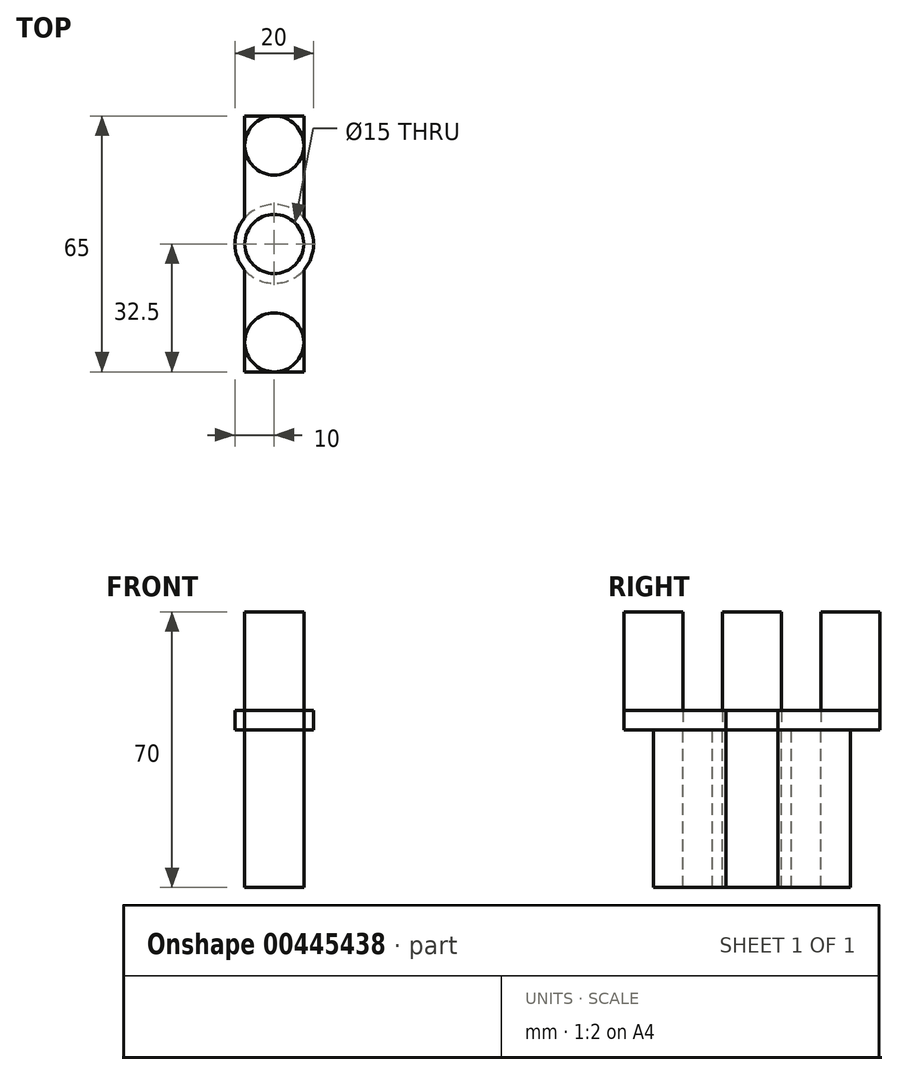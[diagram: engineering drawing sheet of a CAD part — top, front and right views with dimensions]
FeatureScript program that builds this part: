
annotation { "Feature Type Name" : "Feature", "Feature Type Description" : "" }
export const myFeature = defineFeature(function(context is Context, id is Id, definition is map)
    precondition{}
    {
        {
            var Q0;
            Q0=qCreatedBy(makeId("Top.planeOp"),FACE);
            var sketch = newSketch(context, id + "F0", { "sketchPlane" : qUnion([Q0])});
            skLineSegment(sketch, "E0.bottom", {"start": v(-7.5, 32.5) * mm, "end": v(7.5, 32.5) * mm});
            skLineSegment(sketch, "E0.top", {"start": v(-7.5, -32.5) * mm, "end": v(7.5, -32.5) * mm});
            skLineSegment(sketch, "E0.left", {"start": v(-7.5, 32.5) * mm, "end": v(-7.5, -32.5) * mm});
            skLineSegment(sketch, "E0.right", {"start": v(7.5, 32.5) * mm, "end": v(7.5, -32.5) * mm});
            skPoint(sketch, "E0.middle", {"position": v(0, 0) * mm});
            skCircle(sketch, "E1", {"center": v(0, 0) * mm, "radius": 7.5 * mm});
            skCircle(sketch, "E2", {"center": v(0, 25) * mm, "radius": 7.5 * mm});
            skCircle(sketch, "E3", {"center": v(0, -25) * mm, "radius": 7.5 * mm});
            skCircle(sketch, "E4", {"center": v(0, 0) * mm, "radius": 10 * mm});
            skSolve(sketch);
        }
        {
            var Q0;
            Q0 = qSketchRegion(id + "F0", true);
            extrude(context, id + "F1", {"entities" : qUnion([Q0]), "depth" : 5 * mm});
        }
        {
            var Q0;
            {var subQ0=sQuery(id+"F0.wireOp",EDGE,"E1");var subQ1=makeQuery(id+"F0.imprint","INTERSECT",VERTEX,{"derivedFrom":[sQuery(id+"F0.wireOp",EDGE,"E0.left"),subQ0]});Q0=makeQuery(id+"F0.imprint","IMPRINT",FACE,{"disambiguationData":[TD([[makeQuery(id+"F0.imprint","IMPRINT",EDGE,{"disambiguationData":[TD([[subQ1,1.0]])],"derivedFrom":subQ0}),1.0]])]});}
            var Q1;
            {var subQ0=sQuery(id+"F0.wireOp",EDGE,"E3");var subQ1=makeQuery(id+"F0.imprint","INTERSECT",VERTEX,{"derivedFrom":[sQuery(id+"F0.wireOp",EDGE,"E0.left"),subQ0]});Q1=makeQuery(id+"F0.imprint","IMPRINT",FACE,{"disambiguationData":[TD([[makeQuery(id+"F0.imprint","IMPRINT",EDGE,{"disambiguationData":[TD([[subQ1,1.0]])],"derivedFrom":subQ0}),1.0]])]});}
            var Q2;
            {var subQ0=sQuery(id+"F0.wireOp",EDGE,"E2");var subQ1=makeQuery(id+"F0.imprint","INTERSECT",VERTEX,{"derivedFrom":[sQuery(id+"F0.wireOp",EDGE,"E0.bottom"),subQ0]});Q2=makeQuery(id+"F0.imprint","IMPRINT",FACE,{"disambiguationData":[TD([[makeQuery(id+"F0.imprint","IMPRINT",EDGE,{"disambiguationData":[TD([[subQ1,1.0]])],"derivedFrom":subQ0}),1.0]])]});}
            extrude(context, id + "F2", {"entities" : qUnion([Q0, Q1, Q2]), "depth" : 30 * mm});
        }
        {
            var Q0;
            {var subQ0=sQuery(id+"F0.wireOp",EDGE,"E4");var subQ1=sQuery(id+"F0.wireOp",EDGE,"E0.left");var subQ2=makeQuery(id+"F0.imprint","INTERSECT",VERTEX,{"disambiguationData":[OD(0.0)],"derivedFrom":[subQ1,subQ0]});Q0=makeQuery(id+"F0.imprint","IMPRINT",FACE,{"disambiguationData":[TD([[makeQuery(id+"F0.imprint","IMPRINT",EDGE,{"disambiguationData":[TD([[subQ2,-1.0]])],"derivedFrom":subQ1}),-1.0]])]});}
            var Q1;
            {var subQ0=sQuery(id+"F0.wireOp",EDGE,"E4");var subQ1=sQuery(id+"F0.wireOp",EDGE,"E0.left");var subQ2=makeQuery(id+"F0.imprint","INTERSECT",VERTEX,{"disambiguationData":[OD(0.0)],"derivedFrom":[subQ1,subQ0]});Q1=makeQuery(id+"F0.imprint","IMPRINT",FACE,{"disambiguationData":[TD([[makeQuery(id+"F0.imprint","IMPRINT",EDGE,{"disambiguationData":[TD([[subQ2,-1.0]])],"derivedFrom":subQ1}),1.0]])]});}
            var Q2;
            {var subQ0=sQuery(id+"F0.wireOp",EDGE,"E4");var subQ1=sQuery(id+"F0.wireOp",EDGE,"E0.right");var subQ2=makeQuery(id+"F0.imprint","INTERSECT",VERTEX,{"disambiguationData":[OD(0.0)],"derivedFrom":[subQ1,subQ0]});Q2=makeQuery(id+"F0.imprint","IMPRINT",FACE,{"disambiguationData":[TD([[makeQuery(id+"F0.imprint","IMPRINT",EDGE,{"disambiguationData":[TD([[subQ2,-1.0]])],"derivedFrom":subQ1}),1.0]])]});}
            var Q3;
            {var subQ0=sQuery(id+"F0.wireOp",EDGE,"E4");var subQ1=sQuery(id+"F0.wireOp",EDGE,"E0.left");var subQ2=makeQuery(id+"F0.imprint","INTERSECT",VERTEX,{"disambiguationData":[OD(1.0)],"derivedFrom":[subQ1,subQ0]});Q3=makeQuery(id+"F0.imprint","IMPRINT",FACE,{"disambiguationData":[TD([[makeQuery(id+"F0.imprint","IMPRINT",EDGE,{"disambiguationData":[TD([[subQ2,1.0]])],"derivedFrom":subQ1}),1.0]])]});}
            var Q4;
            {var subQ0=sQuery(id+"F0.wireOp",EDGE,"E1");var subQ1=makeQuery(id+"F0.imprint","INTERSECT",VERTEX,{"derivedFrom":[sQuery(id+"F0.wireOp",EDGE,"E0.left"),subQ0]});Q4=makeQuery(id+"F0.imprint","IMPRINT",FACE,{"disambiguationData":[TD([[makeQuery(id+"F0.imprint","IMPRINT",EDGE,{"disambiguationData":[TD([[subQ1,1.0]])],"derivedFrom":subQ0}),1.0]])]});}
            extrude(context, id + "F3", {"entities" : qUnion([Q0, Q1, Q2, Q3, Q4]), "oppositeDirection" : true, "depth" : 40 * mm});
        }
    });
